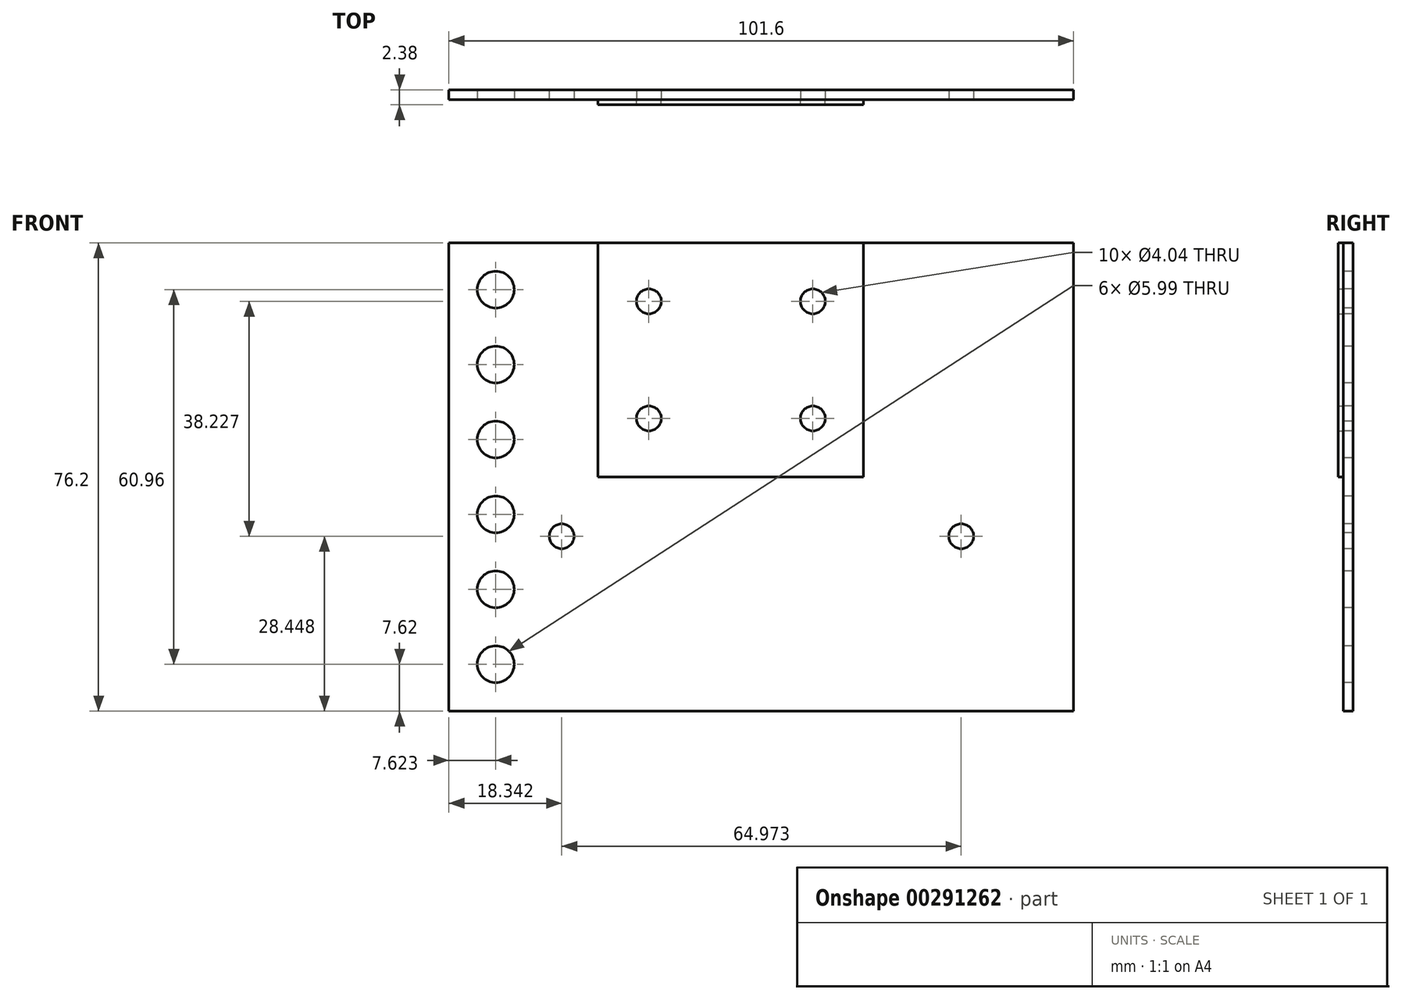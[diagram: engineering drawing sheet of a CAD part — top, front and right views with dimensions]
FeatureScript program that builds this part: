
annotation { "Feature Type Name" : "Feature", "Feature Type Description" : "" }
export const myFeature = defineFeature(function(context is Context, id is Id, definition is map)
    precondition{}
    {
        {
            var Q0;
            Q0=qCreatedBy(makeId("Front.planeOp"),FACE);
            var sketch = newSketch(context, id + "F0", { "sketchPlane" : qUnion([Q0])});
            skLineSegment(sketch, "E0.bottom", {"start": v(-39.8, 38.1) * mm, "end": v(61.8, 38.1) * mm});
            skLineSegment(sketch, "E0.top", {"start": v(-39.8, -38.1) * mm, "end": v(61.8, -38.1) * mm});
            skLineSegment(sketch, "E0.left", {"start": v(-39.8, 38.1) * mm, "end": v(-39.8, -38.1) * mm});
            skLineSegment(sketch, "E0.right", {"start": v(61.8, 38.1) * mm, "end": v(61.8, -38.1) * mm});
            skCircle(sketch, "E1", {"center": v(-32.19, 30.48) * mm, "radius": 3 * mm});
            skCircle(sketch, "E2.1.0.0", {"center": v(-32.19, 18.29) * mm, "radius": 3 * mm});
            skCircle(sketch, "E2.2.0.0", {"center": v(-32.19, 6.1) * mm, "radius": 3 * mm});
            skCircle(sketch, "E2.3.0.0", {"center": v(-32.19, -6.1) * mm, "radius": 3 * mm});
            skCircle(sketch, "E2.4.0.0", {"center": v(-32.19, -18.29) * mm, "radius": 3 * mm});
            skCircle(sketch, "E2.5.0.0", {"center": v(-32.19, -30.48) * mm, "radius": 3 * mm});
            skLineSegment(sketch, "E2.direction1", {"start": v(-32.19, 30.48) * mm, "end": v(-32.19, 18.29) * mm, "construction": true});
            skCircle(sketch, "E3", {"center": v(-7.3, 28.58) * mm, "radius": 2.02 * mm});
            skCircle(sketch, "E4", {"center": v(19.37, 28.58) * mm, "radius": 2.02 * mm});
            skCircle(sketch, "E5", {"center": v(-7.3, 9.53) * mm, "radius": 2.02 * mm});
            skCircle(sketch, "E6", {"center": v(19.37, 9.53) * mm, "radius": 2.02 * mm});
            skCircle(sketch, "E7", {"center": v(-21.47, -9.65) * mm, "radius": 2.02 * mm});
            skCircle(sketch, "E8", {"center": v(43.5, -9.65) * mm, "radius": 2.02 * mm});
            skLineSegment(sketch, "E9.bottom", {"start": v(-15.55, 38.1) * mm, "end": v(27.63, 38.1) * mm});
            skLineSegment(sketch, "E9.top", {"start": v(-15.55, 0) * mm, "end": v(27.63, 0) * mm});
            skLineSegment(sketch, "E9.left", {"start": v(-15.55, 38.1) * mm, "end": v(-15.55, 0) * mm});
            skLineSegment(sketch, "E9.right", {"start": v(27.63, 38.1) * mm, "end": v(27.63, 0) * mm});
            skSolve(sketch);
        }
        {
            var Q0;
            Q0=makeQuery(id+"F0.imprint","IMPRINT",FACE,{"disambiguationData":[TD([[makeQuery(id+"F0.imprint","IMPRINT",EDGE,{"derivedFrom":sQuery(id+"F0.wireOp",EDGE,"E3")}),-1.0]])]});
            extrude(context, id + "F1", {"entities" : qUnion([Q0]), "depth" : 0.8 * mm});
        }
        {
            var Q0;
            Q0=makeQuery(id+"F0.imprint","IMPRINT",FACE,{"disambiguationData":[TD([[makeQuery(id+"F0.imprint","IMPRINT",EDGE,{"derivedFrom":sQuery(id+"F0.wireOp",EDGE,"E0.top")}),1.0]])]});
            var Q1;
            Q1=makeQuery(id+"F0.imprint","IMPRINT",FACE,{"disambiguationData":[TD([[makeQuery(id+"F0.imprint","IMPRINT",EDGE,{"derivedFrom":sQuery(id+"F0.wireOp",EDGE,"E3")}),-1.0]])]});
            extrude(context, id + "F2", {"entities" : qUnion([Q0, Q1]), "oppositeDirection" : true, "depth" : 1.59 * mm});
        }
    });
